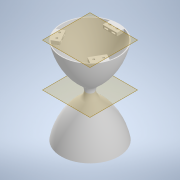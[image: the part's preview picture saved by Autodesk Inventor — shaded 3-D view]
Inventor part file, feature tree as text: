
AUTODESK INVENTOR PART (.ipt)
format: ipt  version: 2020.2 (Build 242310000, 310)  size: 483,328 bytes
history: native  units: in
note: dims shown in document units (in); Inventor stores cm internally (conversion verified against a paired STEP export)
features: sketch x4, extrude x3, fillet x2, plane x2, revolve x1, shell x1, pattern_circular x1, mirror x1
ambient origin geometry x8: Origin, YZ Plane, XZ Plane, XY Plane, X Axis, Y Axis, Z Axis, Center Point
bodies: Solid1 (feature_tree)
feature tree (15):
  revolve  "Revolution1"  [1 undecoded]
  fillet  "Fillet1"  Radius=0.3937in
  shell  "Shell2"  Thickness=3.4038in
  extrude  "Extrusion1"  Depth=4.7244in
  plane  "Work Plane2"
  extrude  "Extrusion3"  Depth=0.3937in
  extrude  "Extrusion4"  Depth=0.0394in
  fillet  "Fillet2"  Radius=0.1969in
  pattern_circular  "Circular Pattern2"  Angle=90.0deg  [1 undecoded]
  plane  "Work Plane3"
  mirror  "Mirror1"
  sketch  "Sketch3"  dims[d39=2.7559in d40=1.5748in d41=4.7244in d42=0.3937in d43=2.1654in d49=3.4038in]
  sketch  "Sketch4"  dims[d50=3.1496in d51=4.7244in]
  sketch  "Sketch6"  dims[d52=2.1654in d54=0.3937in]
  sketch  "Sketch7"  dims[d55=0.1969in d58=0.1969in d59=0.1969in d60=90.0deg d61=0.4537in d63=0.0472in d65=0.3937in d66=0.7874in d67=0.3937in d68=0.1969in d69=0.0in d83=0.0in d84=0.1181in d85=0.1181in d86=0.1969in d87=0.1969in d88=0.1969in d89=0.1969in d90=0.2362in d91=0.0in d92=0.2165in d93=0.0709in d94=0.1181in d95=0.0394in d96=0.0492in d97=0.0157in d99=0.063in d100=0.1378in d101=0.2165in d102=0.0709in d103=0.1181in d104=0.0394in d105=0.0492in d106=0.0157in d107=0.063in d108=0.1378in d109=0.3051in d110=0.0in d111=0.0394in d112=1.1811in d113=360.0deg d115=2.3622in]
note: 2 required parameter values undecoded (feature->parameter linkage not recoverable at this tier; creation-order binding heuristic only, values carry confidence <= 0.55)